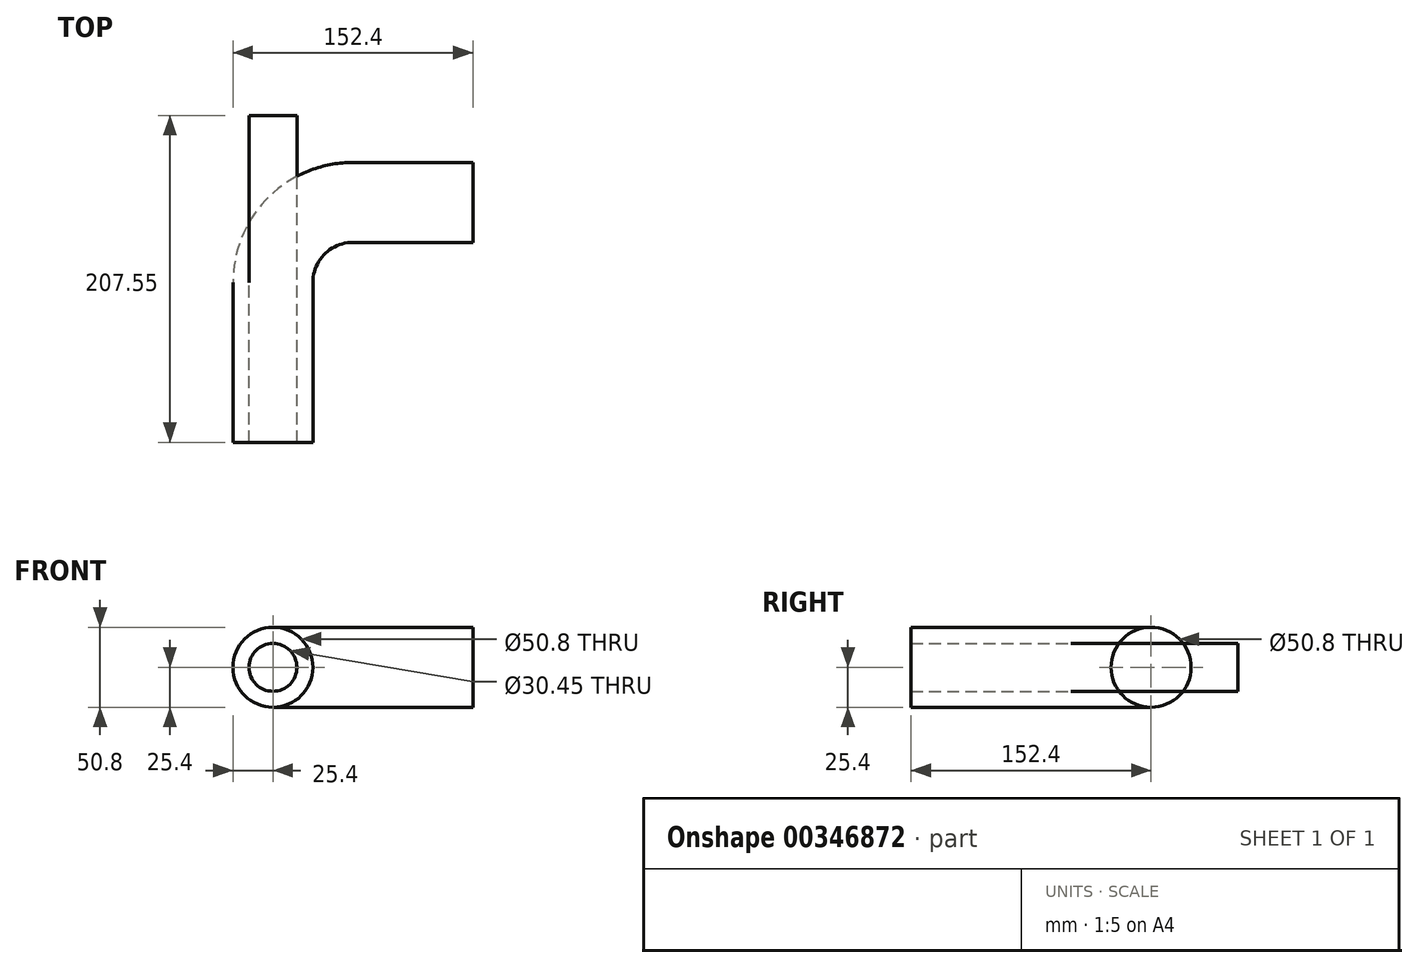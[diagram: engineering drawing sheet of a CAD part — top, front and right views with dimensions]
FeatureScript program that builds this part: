
annotation { "Feature Type Name" : "Feature", "Feature Type Description" : "" }
export const myFeature = defineFeature(function(context is Context, id is Id, definition is map)
    precondition{}
    {
        {
            var Q0;
            Q0=qCreatedBy(makeId("Top.planeOp"),FACE);
            var sketch = newSketch(context, id + "F0", { "sketchPlane" : qUnion([Q0])});
            skLineSegment(sketch, "E0", {"start": v(0, 0) * mm, "end": v(0, 101.6) * mm});
            skLineSegment(sketch, "E1", {"start": v(50.8, 152.4) * mm, "end": v(127, 152.4) * mm});
            skPoint(sketch, "E2.visualSharp", {"position": v(0, 152.4) * mm});
            skArc(sketch, "E2.filletArc", {"start": v(50.8, 152.4) * mm, "mid": v(14.88, 137.52) * mm, "end": v(0, 101.6) * mm});
            skSolve(sketch);
        }
        {
            var Q0;
            Q0=qCreatedBy(makeId("Front.planeOp"),FACE);
            var sketch = newSketch(context, id + "F1", { "sketchPlane" : qUnion([Q0])});
            skCircle(sketch, "E3", {"center": v(0, 0) * mm, "radius": 25.4 * mm});
            skSolve(sketch);
        }
        {
            var Q0;
            Q0=makeQuery(id+"F1.imprint","IMPRINT",FACE,{"disambiguationData":[TD([[makeQuery(id+"F1.imprint","IMPRINT",EDGE,{"derivedFrom":sQuery(id+"F1.wireOp",EDGE,"E3")}),1.0]])]});
            var Q1;
            Q1=sQuery(id+"F1.wireOp",EDGE,"E3");
            var Q2;
            Q2=sQuery(id+"F0.wireOp",EDGE,"E0");
            var Q3;
            Q3=sQuery(id+"F0.wireOp",EDGE,"E2.filletArc");
            var Q4;
            Q4=sQuery(id+"F0.wireOp",EDGE,"E1");
            sweep(context, id + "F2", {"bodyType" : ToolBodyType.SURFACE, "profiles" : qUnion([Q0]), "surfaceProfiles" : qUnion([Q1]), "path" : qUnion([Q2, Q3, Q4])});
        }
        {
            var Q0;
            Q0=qCreatedBy(makeId("Front.planeOp"),FACE);
            var sketch = newSketch(context, id + "F3", { "sketchPlane" : qUnion([Q0])});
            skCircle(sketch, "E4", {"center": v(0, 0) * mm, "radius": 15.23 * mm});
            skSolve(sketch);
        }
        {
            var Q0;
            Q0 = qSketchRegion(id + "F3", true);
            var Q1;
            Q1=sQuery(id+"F3.wireOp",EDGE,"E4");
            extrude(context, id + "F4", {"entities" : qUnion([Q0]), "bodyType" : ToolBodyType.SURFACE, "surfaceEntities" : qUnion([Q1]), "oppositeDirection" : true, "depth" : 207.55 * mm});
        }
    });
